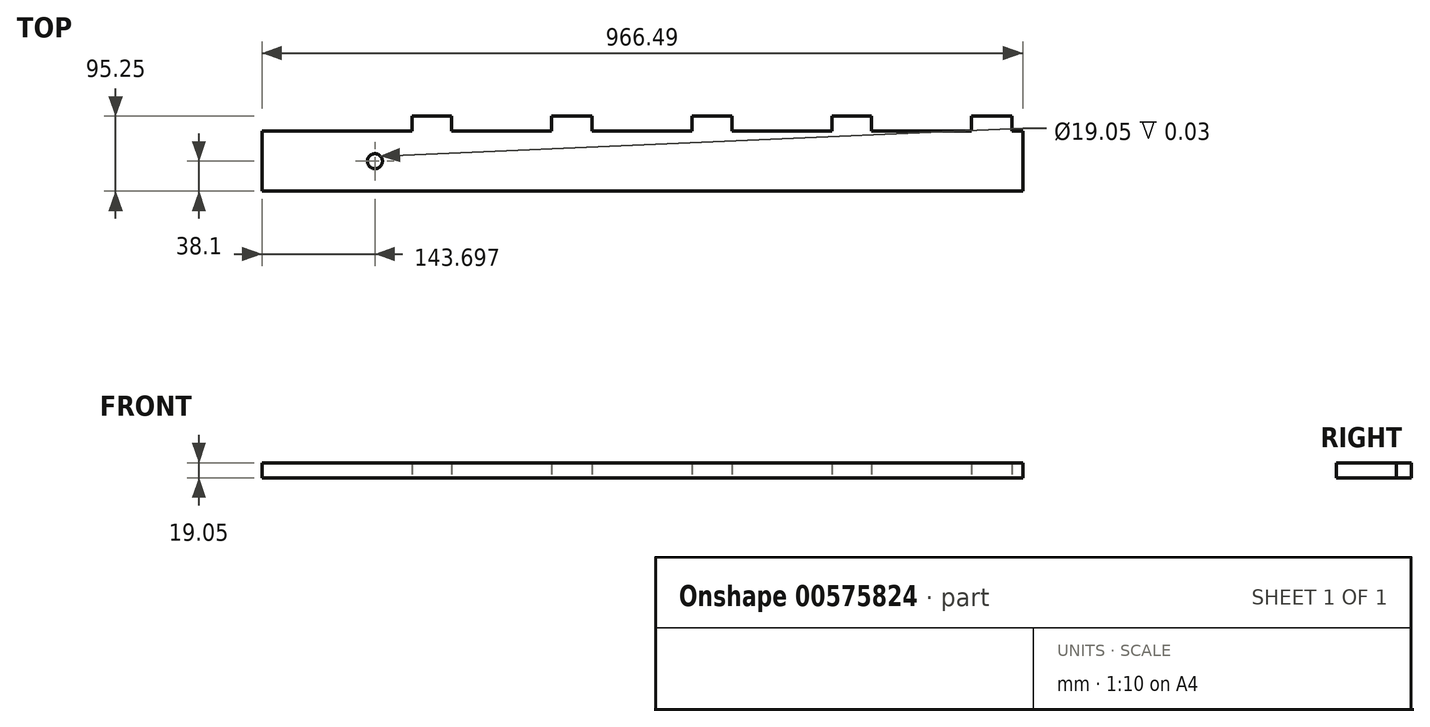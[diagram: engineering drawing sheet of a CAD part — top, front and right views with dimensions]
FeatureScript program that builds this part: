
annotation { "Feature Type Name" : "Feature", "Feature Type Description" : "" }
export const myFeature = defineFeature(function(context is Context, id is Id, definition is map)
    precondition{}
    {
        {
            var Q0;
            Q0=qCreatedBy(makeId("Top.planeOp"),FACE);
            var sketch = newSketch(context, id + "F0", { "sketchPlane" : qUnion([Q0])});
            skLineSegment(sketch, "E0.bottom", {"start": v(0, 0) * mm, "end": v(1143, 0) * mm});
            skLineSegment(sketch, "E0.top", {"start": v(0, -76.2) * mm, "end": v(1143, -76.2) * mm});
            skLineSegment(sketch, "E0.left", {"start": v(0, 0) * mm, "end": v(0, -76.2) * mm});
            skLineSegment(sketch, "E0.right", {"start": v(1143, 0) * mm, "end": v(1143, -76.2) * mm});
            skSolve(sketch);
        }
        {
            var Q0;
            Q0=makeQuery(id+"F0.imprint","IMPRINT",FACE,{"disambiguationData":[TD([[makeQuery(id+"F0.imprint","IMPRINT",EDGE,{"derivedFrom":sQuery(id+"F0.wireOp",EDGE,"E0.bottom")}),-1.0]])]});
            extrude(context, id + "F1", {"entities" : qUnion([Q0]), "depth" : 19.05 * mm, "offsetDistance" : 25.4 * mm});
        }
        {
            var Q0;
            Q0=makeQuery(id+"F1.opExtrude","SWEPT_FACE",FACE,{"disambiguationData":[OSD([sQuery(id+"F0.wireOp",EDGE,"E0.bottom")])]});
            var sketch = newSketch(context, id + "F2", { "sketchPlane" : qUnion([Q0])});
            skLineSegment(sketch, "E1.bottom", {"start": v(-952.5, 19.05) * mm, "end": v(-901.7, 19.05) * mm});
            skLineSegment(sketch, "E1.top", {"start": v(-952.5, 0) * mm, "end": v(-901.7, 0) * mm});
            skLineSegment(sketch, "E1.left", {"start": v(-952.5, 19.05) * mm, "end": v(-952.5, 0) * mm});
            skLineSegment(sketch, "E1.right", {"start": v(-901.7, 19.05) * mm, "end": v(-901.7, 0) * mm});
            skLineSegment(sketch, "E2.bottom", {"start": v(-774.7, 19.05) * mm, "end": v(-723.9, 19.05) * mm});
            skLineSegment(sketch, "E2.top", {"start": v(-774.7, 0) * mm, "end": v(-723.9, 0) * mm});
            skLineSegment(sketch, "E2.left", {"start": v(-774.7, 19.05) * mm, "end": v(-774.7, 0) * mm});
            skLineSegment(sketch, "E2.right", {"start": v(-723.9, 19.05) * mm, "end": v(-723.9, 0) * mm});
            skLineSegment(sketch, "E3.bottom", {"start": v(-596.9, 19.05) * mm, "end": v(-546.1, 19.05) * mm});
            skLineSegment(sketch, "E3.top", {"start": v(-596.9, 0) * mm, "end": v(-546.1, 0) * mm});
            skLineSegment(sketch, "E3.left", {"start": v(-596.9, 19.05) * mm, "end": v(-596.9, 0) * mm});
            skLineSegment(sketch, "E3.right", {"start": v(-546.1, 19.05) * mm, "end": v(-546.1, 0) * mm});
            skLineSegment(sketch, "E4.bottom", {"start": v(-419.1, 19.05) * mm, "end": v(-368.3, 19.05) * mm});
            skLineSegment(sketch, "E4.top", {"start": v(-419.1, 0) * mm, "end": v(-368.3, 0) * mm});
            skLineSegment(sketch, "E4.left", {"start": v(-419.1, 19.05) * mm, "end": v(-419.1, 0) * mm});
            skLineSegment(sketch, "E4.right", {"start": v(-368.3, 19.05) * mm, "end": v(-368.3, 0) * mm});
            skLineSegment(sketch, "E5.bottom", {"start": v(-241.3, 19.05) * mm, "end": v(-190.5, 19.05) * mm});
            skLineSegment(sketch, "E5.top", {"start": v(-241.3, 0) * mm, "end": v(-190.5, 0) * mm});
            skLineSegment(sketch, "E5.left", {"start": v(-241.3, 19.05) * mm, "end": v(-241.3, 0) * mm});
            skLineSegment(sketch, "E5.right", {"start": v(-190.5, 19.05) * mm, "end": v(-190.5, 0) * mm});
            skSolve(sketch);
        }
        {
            var Q0;
            Q0=makeQuery(id+"F2.imprint","IMPRINT",FACE,{"disambiguationData":[TD([[makeQuery(id+"F2.imprint","IMPRINT",EDGE,{"derivedFrom":sQuery(id+"F2.wireOp",EDGE,"E1.bottom")}),1.0]])]});
            var Q1;
            Q1=makeQuery(id+"F2.imprint","IMPRINT",FACE,{"disambiguationData":[TD([[makeQuery(id+"F2.imprint","IMPRINT",EDGE,{"derivedFrom":sQuery(id+"F2.wireOp",EDGE,"E2.bottom")}),1.0]])]});
            var Q2;
            Q2=makeQuery(id+"F2.imprint","IMPRINT",FACE,{"disambiguationData":[TD([[makeQuery(id+"F2.imprint","IMPRINT",EDGE,{"derivedFrom":sQuery(id+"F2.wireOp",EDGE,"E3.bottom")}),1.0]])]});
            var Q3;
            Q3=makeQuery(id+"F2.imprint","IMPRINT",FACE,{"disambiguationData":[TD([[makeQuery(id+"F2.imprint","IMPRINT",EDGE,{"derivedFrom":sQuery(id+"F2.wireOp",EDGE,"E4.bottom")}),1.0]])]});
            var Q4;
            Q4=makeQuery(id+"F2.imprint","IMPRINT",FACE,{"disambiguationData":[TD([[makeQuery(id+"F2.imprint","IMPRINT",EDGE,{"derivedFrom":sQuery(id+"F2.wireOp",EDGE,"E5.bottom")}),1.0]])]});
            extrude(context, id + "F3", {"entities" : qUnion([Q0, Q1, Q2, Q3, Q4]), "operationType" : NewBodyOperationType.ADD, "depth" : 19.05 * mm, "offsetDistance" : 25.4 * mm});
        }
        {
            var Q0;
            Q0=makeQuery(id+"F3.boolean.opBoolean","MERGE",FACE,{"derivedFrom":[makeQuery(id+"F1.opExtrude","CAP_FACE",FACE,{"disambiguationData":[OSD([sQuery(id+"F0.wireOp",EDGE,"E0.bottom"),sQuery(id+"F0.wireOp",EDGE,"E0.top"),sQuery(id+"F0.wireOp",EDGE,"E0.left"),sQuery(id+"F0.wireOp",EDGE,"E0.right")])],"isStart":false}),makeQuery(id+"F3.opExtrude","SWEPT_FACE",FACE,{"disambiguationData":[OSD([sQuery(id+"F2.wireOp",EDGE,"E1.bottom")])]}),makeQuery(id+"F3.opExtrude","SWEPT_FACE",FACE,{"disambiguationData":[OSD([sQuery(id+"F2.wireOp",EDGE,"E2.bottom")])]}),makeQuery(id+"F3.opExtrude","SWEPT_FACE",FACE,{"disambiguationData":[OSD([sQuery(id+"F2.wireOp",EDGE,"E3.bottom")])]}),makeQuery(id+"F3.opExtrude","SWEPT_FACE",FACE,{"disambiguationData":[OSD([sQuery(id+"F2.wireOp",EDGE,"E4.bottom")])]}),makeQuery(id+"F3.opExtrude","SWEPT_FACE",FACE,{"disambiguationData":[OSD([sQuery(id+"F2.wireOp",EDGE,"E5.bottom")])]})]});
            var sketch = newSketch(context, id + "F4", { "sketchPlane" : qUnion([Q0])});
            skLineSegment(sketch, "E6", {"start": v(190.5, 0) * mm, "end": v(190.5, -76.2) * mm, "construction": true});
            skLineSegment(sketch, "E7", {"start": v(143.7, -38.1) * mm, "end": v(190.5, -38.1) * mm, "construction": true});
            skCircle(sketch, "E8", {"center": v(143.7, -38.1) * mm, "radius": 9.53 * mm});
            skSolve(sketch);
        }
        {
            var Q0;
            Q0=makeQuery(id+"F4.imprint","IMPRINT",FACE,{"disambiguationData":[TD([[makeQuery(id+"F4.imprint","IMPRINT",EDGE,{"derivedFrom":sQuery(id+"F4.wireOp",EDGE,"E8")}),1.0]])]});
            extrude(context, id + "F5", {"entities" : qUnion([Q0]), "operationType" : NewBodyOperationType.REMOVE, "oppositeDirection" : true, "depth" : 3 / 101.6 * mm, "offsetDistance" : 25.4 * mm});
        }
        {
            var Q0;
            Q0=makeQuery(id+"F3.boolean.opBoolean","MERGE",FACE,{"derivedFrom":[makeQuery(id+"F1.opExtrude","CAP_FACE",FACE,{"disambiguationData":[OSD([sQuery(id+"F0.wireOp",EDGE,"E0.bottom"),sQuery(id+"F0.wireOp",EDGE,"E0.top"),sQuery(id+"F0.wireOp",EDGE,"E0.left"),sQuery(id+"F0.wireOp",EDGE,"E0.right")])],"isStart":false}),makeQuery(id+"F3.opExtrude","SWEPT_FACE",FACE,{"disambiguationData":[OSD([sQuery(id+"F2.wireOp",EDGE,"E1.bottom")])]}),makeQuery(id+"F3.opExtrude","SWEPT_FACE",FACE,{"disambiguationData":[OSD([sQuery(id+"F2.wireOp",EDGE,"E2.bottom")])]}),makeQuery(id+"F3.opExtrude","SWEPT_FACE",FACE,{"disambiguationData":[OSD([sQuery(id+"F2.wireOp",EDGE,"E3.bottom")])]}),makeQuery(id+"F3.opExtrude","SWEPT_FACE",FACE,{"disambiguationData":[OSD([sQuery(id+"F2.wireOp",EDGE,"E4.bottom")])]}),makeQuery(id+"F3.opExtrude","SWEPT_FACE",FACE,{"disambiguationData":[OSD([sQuery(id+"F2.wireOp",EDGE,"E5.bottom")])]})]});
            var sketch = newSketch(context, id + "F6", { "sketchPlane" : qUnion([Q0])});
            skLineSegment(sketch, "E9", {"start": v(1143, 0) * mm, "end": v(1047.75, 0) * mm, "construction": true});
            skLineSegment(sketch, "E10.bottom", {"start": v(1059.18, -15.87) * mm, "end": v(1036.32, -15.87) * mm});
            skLineSegment(sketch, "E10.top", {"start": v(1059.18, 15.88) * mm, "end": v(1036.32, 15.88) * mm});
            skLineSegment(sketch, "E10.left", {"start": v(1059.18, -15.87) * mm, "end": v(1059.18, 15.88) * mm});
            skLineSegment(sketch, "E10.right", {"start": v(1036.32, -15.87) * mm, "end": v(1036.32, 15.88) * mm});
            skPoint(sketch, "E10.middle", {"position": v(1047.75, 0) * mm});
            skSolve(sketch);
        }
        {
            var Q0;
            Q0=makeQuery(id+"F6.imprint","IMPRINT",FACE,{"disambiguationData":[TD([[makeQuery(id+"F6.imprint","IMPRINT",EDGE,{"derivedFrom":sQuery(id+"F6.wireOp",EDGE,"Se9C1wWy-YAoU-u63g-tAUS-tnV8TLcbua2C")}),1.0]])]});
            var Q1;
            {var subQ0=sQuery(id+"F6.wireOp",EDGE,"E10.bottom");Q1=makeQuery(id+"F6.imprint","IMPRINT",FACE,{"disambiguationData":[TD([[makeQuery(id+"F6.imprint","IMPRINT",EDGE,{"derivedFrom":subQ0}),-1.0]])]});}
            extrude(context, id + "F7", {"entities" : qUnion([Q0, Q1]), "operationType" : NewBodyOperationType.REMOVE, "oppositeDirection" : true, "depth" : 25.4 * mm, "offsetDistance" : 25.4 * mm});
        }
        {
            var Q0;
            Q0=makeQuery(id+"F3.boolean.opBoolean","MERGE",FACE,{"derivedFrom":[makeQuery(id+"F1.opExtrude","CAP_FACE",FACE,{"disambiguationData":[OSD([sQuery(id+"F0.wireOp",EDGE,"E0.bottom"),sQuery(id+"F0.wireOp",EDGE,"E0.top"),sQuery(id+"F0.wireOp",EDGE,"E0.left"),sQuery(id+"F0.wireOp",EDGE,"E0.right")])],"isStart":false}),makeQuery(id+"F3.opExtrude","SWEPT_FACE",FACE,{"disambiguationData":[OSD([sQuery(id+"F2.wireOp",EDGE,"E1.bottom")])]}),makeQuery(id+"F3.opExtrude","SWEPT_FACE",FACE,{"disambiguationData":[OSD([sQuery(id+"F2.wireOp",EDGE,"E2.bottom")])]}),makeQuery(id+"F3.opExtrude","SWEPT_FACE",FACE,{"disambiguationData":[OSD([sQuery(id+"F2.wireOp",EDGE,"E3.bottom")])]}),makeQuery(id+"F3.opExtrude","SWEPT_FACE",FACE,{"disambiguationData":[OSD([sQuery(id+"F2.wireOp",EDGE,"E4.bottom")])]}),makeQuery(id+"F3.opExtrude","SWEPT_FACE",FACE,{"disambiguationData":[OSD([sQuery(id+"F2.wireOp",EDGE,"E5.bottom")])]})]});
            var sketch = newSketch(context, id + "F8", { "sketchPlane" : qUnion([Q0])});
            skLineSegment(sketch, "E11.bottom", {"start": v(966.49, 19.05) * mm, "end": v(1154.38, 19.05) * mm});
            skLineSegment(sketch, "E11.top", {"start": v(966.49, -108.92) * mm, "end": v(1154.38, -108.92) * mm});
            skLineSegment(sketch, "E11.left", {"start": v(966.49, 19.05) * mm, "end": v(966.49, -108.92) * mm});
            skLineSegment(sketch, "E11.right", {"start": v(1154.38, 19.05) * mm, "end": v(1154.38, -108.92) * mm});
            skSolve(sketch);
        }
        {
            var Q0;
            {var subQ1=sQuery(id+"F0.wireOp",EDGE,"E0.right");var subQ2=makeQuery(id+"F1.opExtrude","CAP_EDGE",EDGE,{"disambiguationData":[OSD([subQ1])],"isStart":false});Q0=makeQuery(id+"F8.imprint","IMPRINT",FACE,{"disambiguationData":[TD([[makeQuery(id+"F8.imprint","IMPRINT",EDGE,{"derivedFrom":subQ2}),-1.0]])]});}
            extrude(context, id + "F9", {"entities" : qUnion([Q0]), "operationType" : NewBodyOperationType.REMOVE, "oppositeDirection" : true, "depth" : 25.4 * mm, "offsetDistance" : 25.4 * mm});
        }
    });
